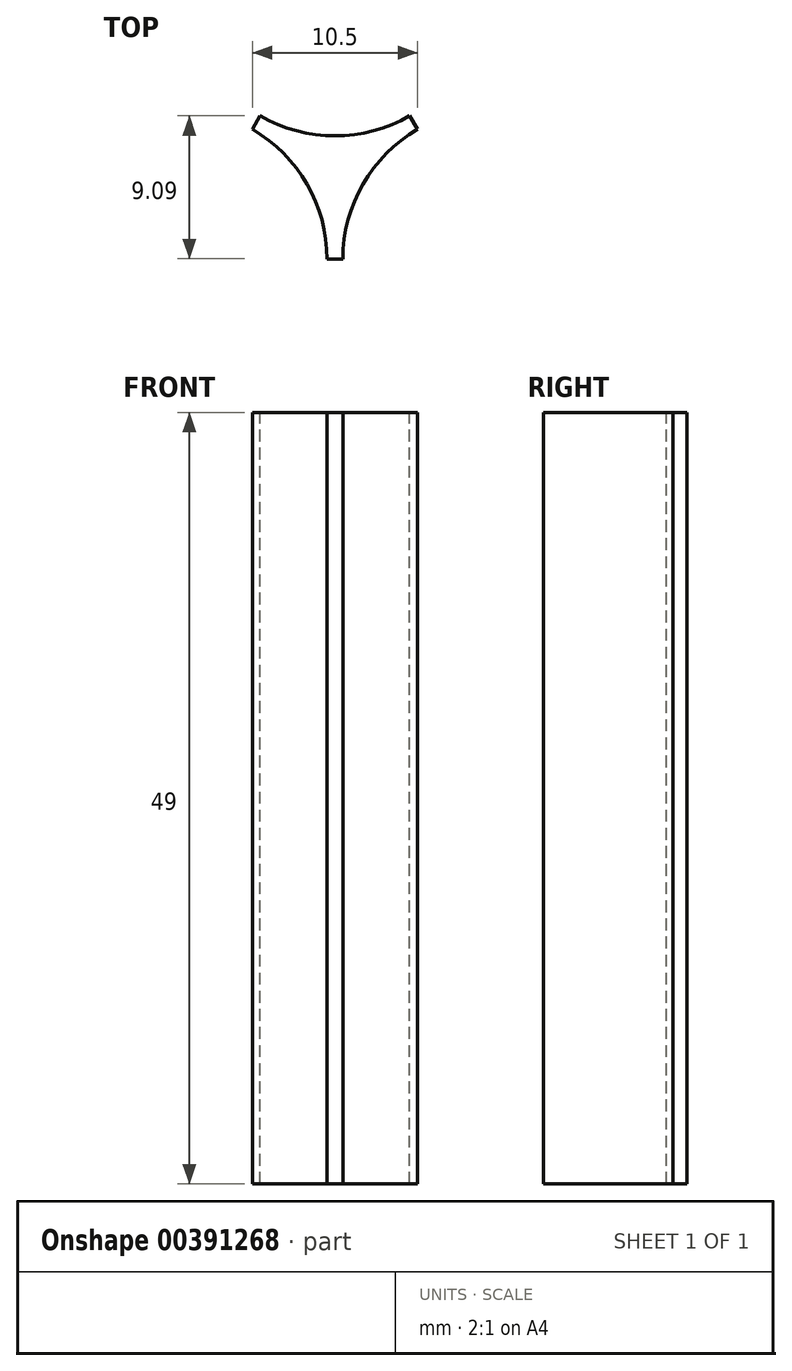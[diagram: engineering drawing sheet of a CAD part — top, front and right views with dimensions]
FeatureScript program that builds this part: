
annotation { "Feature Type Name" : "Feature", "Feature Type Description" : "" }
export const myFeature = defineFeature(function(context is Context, id is Id, definition is map)
    precondition{}
    {
        {
            var Q0;
            Q0=qCreatedBy(makeId("Top.planeOp"),FACE);
            var sketch = newSketch(context, id + "F0", { "sketchPlane" : qUnion([Q0])});
            skCircle(sketch, "E0", {"center": v(-10, -5.77) * mm, "radius": 9.5 * mm});
            skCircle(sketch, "E1.1.0.0", {"center": v(10, -5.77) * mm, "radius": 9.5 * mm});
            skLineSegment(sketch, "E1.direction1", {"start": v(-10, -5.77) * mm, "end": v(10, -5.77) * mm, "construction": true});
            skCircle(sketch, "E2", {"center": v(0, 11.55) * mm, "radius": 9.5 * mm});
            skCircle(sketch, "E3", {"center": v(0, 0) * mm, "radius": 2.05 * mm});
            skLineSegment(sketch, "E4", {"start": v(-4.75, 3.32) * mm, "end": v(-5.25, 2.45) * mm});
            skLineSegment(sketch, "E5", {"start": v(4.75, 3.32) * mm, "end": v(5.25, 2.45) * mm});
            skLineSegment(sketch, "E6", {"start": v(0.5, -5.77) * mm, "end": v(-0.5, -5.77) * mm});
            skPoint(sketch, "E6.startSnap0", {"position": v(0, -5.77) * mm});
            skLineSegment(sketch, "E7", {"start": v(-10, -5.77) * mm, "end": v(0, 11.55) * mm, "construction": true});
            skLineSegment(sketch, "E8", {"start": v(10, -5.77) * mm, "end": v(0, 11.55) * mm, "construction": true});
            skSolve(sketch);
        }
        {
            var Q0;
            {var subQ0=sQuery(id+"F0.wireOp",EDGE,"E6");Q0=makeQuery(id+"F0.imprint","IMPRINT",FACE,{"disambiguationData":[TD([[makeQuery(id+"F0.imprint","IMPRINT",EDGE,{"derivedFrom":subQ0}),-1.0]])]});}
            var Q1;
            {var subQ0=sQuery(id+"F0.wireOp",EDGE,"E4");Q1=makeQuery(id+"F0.imprint","IMPRINT",FACE,{"disambiguationData":[TD([[makeQuery(id+"F0.imprint","IMPRINT",EDGE,{"derivedFrom":subQ0}),1.0]])]});}
            var Q2;
            {var subQ0=sQuery(id+"F0.wireOp",EDGE,"E3");var subQ1=makeQuery(id+"F0.imprint","INTERSECT",VERTEX,{"derivedFrom":[sQuery(id+"F0.wireOp",EDGE,"E0"),subQ0]});Q2=makeQuery(id+"F0.imprint","IMPRINT",FACE,{"disambiguationData":[TD([[makeQuery(id+"F0.imprint","IMPRINT",EDGE,{"disambiguationData":[TD([[subQ1,1.0]])],"derivedFrom":subQ0}),1.0]])]});}
            var Q3;
            {var subQ0=sQuery(id+"F0.wireOp",EDGE,"E5");Q3=makeQuery(id+"F0.imprint","IMPRINT",FACE,{"disambiguationData":[TD([[makeQuery(id+"F0.imprint","IMPRINT",EDGE,{"derivedFrom":subQ0}),-1.0]])]});}
            extrude(context, id + "F1", {"entities" : qUnion([Q0, Q1, Q2, Q3]), "oppositeDirection" : true, "depth" : (65 - 8 - 8) * mm});
        }
    });
